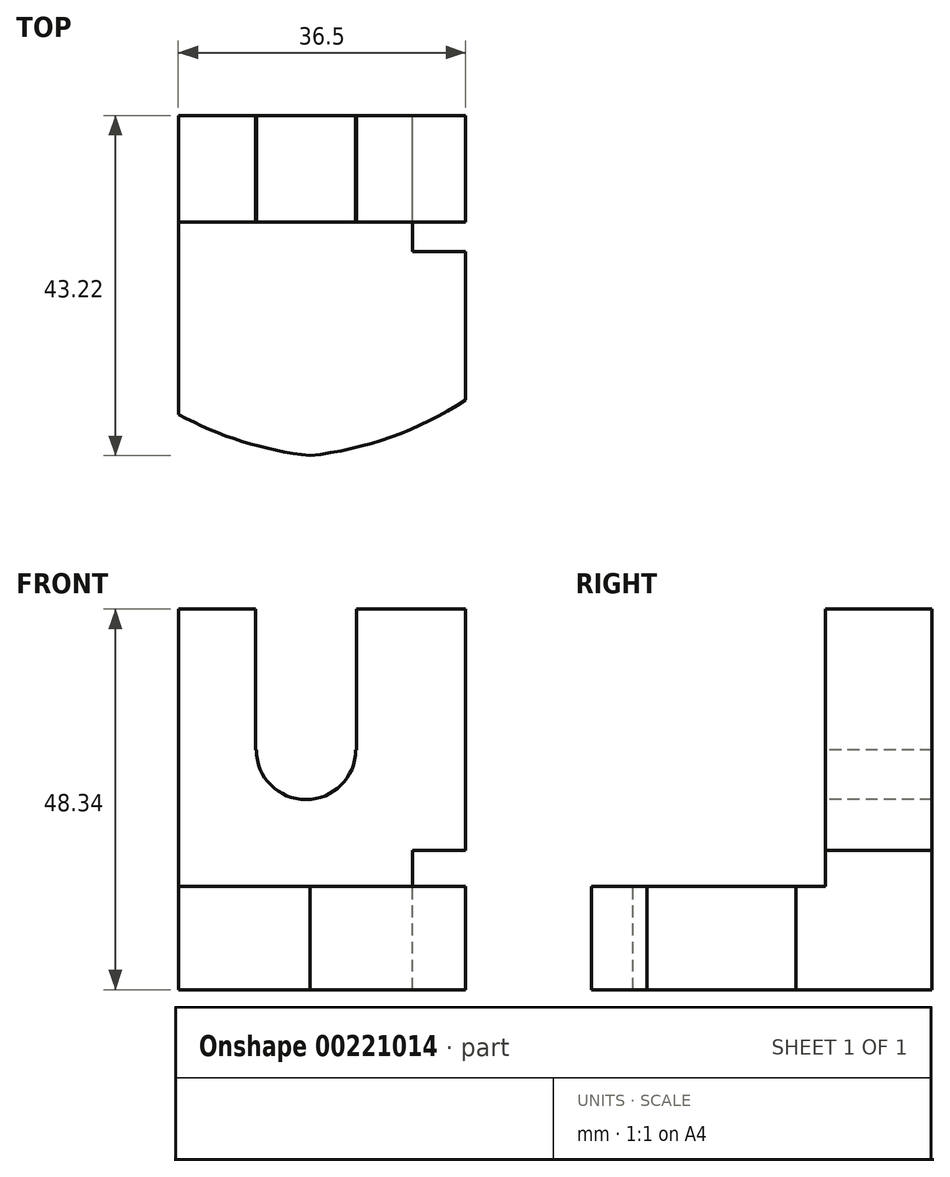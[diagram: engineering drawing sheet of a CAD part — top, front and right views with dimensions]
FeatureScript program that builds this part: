
annotation { "Feature Type Name" : "Feature", "Feature Type Description" : "" }
export const myFeature = defineFeature(function(context is Context, id is Id, definition is map)
    precondition{}
    {
        {
            var Q0;
            Q0=qCreatedBy(makeId("Top.planeOp"),FACE);
            var sketch = newSketch(context, id + "F0", { "sketchPlane" : qUnion([Q0])});
            skLineSegment(sketch, "E0.bottom", {"start": v(26.54, -21.75) * mm, "end": v(-26.54, -21.75) * mm});
            skLineSegment(sketch, "E0.top", {"start": v(26.54, 21.75) * mm, "end": v(-26.54, 21.75) * mm});
            skLineSegment(sketch, "E0.left", {"start": v(26.54, -21.75) * mm, "end": v(26.54, 21.75) * mm});
            skLineSegment(sketch, "E0.right", {"start": v(-26.54, -21.75) * mm, "end": v(-26.54, 21.75) * mm});
            skPoint(sketch, "E0.middle", {"position": v(0, 0) * mm});
            skSolve(sketch);
        }
        {
            var Q0;
            Q0 = qSketchRegion(id + "F0", true);
            var Q1;
            Q1=makeQuery(id+"F0.imprint","IMPRINT",FACE,{"disambiguationData":[TD([[makeQuery(id+"F0.imprint","IMPRINT",EDGE,{"derivedFrom":sQuery(id+"F0.wireOp",EDGE,"E0.bottom")}),-1.0]])]});
            extrude(context, id + "F1", {"entities" : qUnion([Q0, Q1]), "depth" : 48.34 * mm});
        }
        {
            var Q0;
            Q0=makeQuery(id+"F1.opExtrude","SWEPT_FACE",FACE,{"disambiguationData":[OSD([sQuery(id+"F0.wireOp",EDGE,"E0.left")])]});
            var sketch = newSketch(context, id + "F2", { "sketchPlane" : qUnion([Q0])});
            skLineSegment(sketch, "E1.bottom", {"start": v(-21.75, 13.12) * mm, "end": v(8.2, 13.12) * mm});
            skLineSegment(sketch, "E1.top", {"start": v(-21.75, 48.34) * mm, "end": v(8.2, 48.34) * mm});
            skLineSegment(sketch, "E1.left", {"start": v(-21.75, 13.12) * mm, "end": v(-21.75, 48.34) * mm});
            skLineSegment(sketch, "E1.right", {"start": v(8.2, 13.12) * mm, "end": v(8.2, 48.34) * mm});
            skSolve(sketch);
        }
        {
            var Q0;
            Q0=makeQuery(id+"F2.imprint","IMPRINT",FACE,{"disambiguationData":[TD([[makeQuery(id+"F2.imprint","IMPRINT",EDGE,{"derivedFrom":sQuery(id+"F2.wireOp",EDGE,"E1.bottom")}),1.0]])]});
            extrude(context, id + "F3", {"entities" : qUnion([Q0]), "operationType" : NewBodyOperationType.REMOVE, "endBound" : BoundingType.THROUGH_ALL, "oppositeDirection" : true, "depth" : 25.4 * mm});
        }
        {
            var Q0;
            Q0=makeQuery(id+"F3.boolean.opBoolean","COPY",FACE,{"derivedFrom":makeQuery(id+"F3.opExtrude","SWEPT_FACE",FACE,{"disambiguationData":[OSD([sQuery(id+"F2.wireOp",EDGE,"E1.right")])]})});
            var sketch = newSketch(context, id + "F11", { "sketchPlane" : qUnion([Q0])});
            skLineSegment(sketch, "E2.bottom", {"start": v(-6.91, 48.34) * mm, "end": v(5.89, 48.34) * mm});
            skLineSegment(sketch, "E2.top", {"start": v(-6.91, 30.46) * mm, "end": v(5.89, 30.46) * mm});
            skLineSegment(sketch, "E2.left", {"start": v(-6.91, 48.34) * mm, "end": v(-6.91, 30.46) * mm});
            skLineSegment(sketch, "E2.right", {"start": v(5.89, 48.34) * mm, "end": v(5.89, 30.46) * mm});
            skSolve(sketch);
        }
        {
            var Q0;
            Q0 = qSketchRegion(id + "F11", true);
            var Q1;
            Q1=makeQuery(id+"F11.imprint","IMPRINT",FACE,{"disambiguationData":[TD([[makeQuery(id+"F11.imprint","IMPRINT",EDGE,{"derivedFrom":sQuery(id+"F11.wireOp",EDGE,"E2.bottom")}),-1.0]])]});
            extrude(context, id + "F12", {"entities" : qUnion([Q0, Q1]), "operationType" : NewBodyOperationType.REMOVE, "endBound" : BoundingType.THROUGH_ALL, "oppositeDirection" : true, "depth" : 25.4 * mm});
        }
        {
            var Q0;
            Q0=makeQuery(id+"F3.boolean.opBoolean","COPY",FACE,{"derivedFrom":makeQuery(id+"F3.opExtrude","SWEPT_FACE",FACE,{"disambiguationData":[OSD([sQuery(id+"F2.wireOp",EDGE,"E1.right")])]})});
            var sketch = newSketch(context, id + "F13", { "sketchPlane" : qUnion([Q0])});
            skCircle(sketch, "E3", {"center": v(-0.51, 30.46) * mm, "radius": 6.31 * mm});
            skSolve(sketch);
        }
        {
            var Q0;
            Q0 = qSketchRegion(id + "F13", true);
            extrude(context, id + "F4", {"entities" : qUnion([Q0]), "operationType" : NewBodyOperationType.REMOVE, "endBound" : BoundingType.THROUGH_ALL, "oppositeDirection" : true, "depth" : 25.4 * mm});
        }
        {
            var Q0;
            Q0=makeQuery(id+"F1.opExtrude","SWEPT_EDGE",EDGE,{"disambiguationData":[OSD([sQuery(id+"F0.wireOp",EDGE,"E0.bottom"),sQuery(id+"F0.wireOp",EDGE,"E0.left")])]});
            var Q1;
            Q1=makeQuery(id+"F1.opExtrude","SWEPT_EDGE",EDGE,{"disambiguationData":[OSD([sQuery(id+"F0.wireOp",EDGE,"E0.bottom"),sQuery(id+"F0.wireOp",EDGE,"E0.right")])]});
            chamfer(context, id + "F5", {"entities" : qUnion([Q0, Q1]), "width" : 12.7 * mm, "tangentPropagation" : true});
        }
        {
            var Q0;
            {var subQ0=sQuery(id+"F0.wireOp",EDGE,"E0.bottom");Q0=makeQuery(id+"F5.opChamfer","BLEND_EDGE",EDGE,{"blendedFrom":[makeQuery(id+"F1.opExtrude","SWEPT_EDGE",EDGE,{"disambiguationData":[OSD([subQ0,sQuery(id+"F0.wireOp",EDGE,"E0.right")])]}),makeQuery(id+"F1.opExtrude","SWEPT_FACE",FACE,{"disambiguationData":[OSD([subQ0])]})],"blendedInto":[makeQuery(id+"F1.opExtrude","SWEPT_FACE",FACE,{"disambiguationData":[OSD([subQ0])]})]});}
            var Q1;
            {var subQ0=sQuery(id+"F0.wireOp",EDGE,"E0.bottom");Q1=makeQuery(id+"F5.opChamfer","BLEND_EDGE",EDGE,{"blendedFrom":[makeQuery(id+"F1.opExtrude","SWEPT_EDGE",EDGE,{"disambiguationData":[OSD([subQ0,sQuery(id+"F0.wireOp",EDGE,"E0.left")])]}),makeQuery(id+"F1.opExtrude","SWEPT_FACE",FACE,{"disambiguationData":[OSD([subQ0])]})],"blendedInto":[makeQuery(id+"F1.opExtrude","SWEPT_FACE",FACE,{"disambiguationData":[OSD([subQ0])]})]});}
            fillet(context, id + "F14", {"entities" : qUnion([Q0, Q1]), "radius" : 45.67 * mm, "tangentPropagation" : true, "allowEdgeOverflow" : false});
        }
        {
            var Q0;
            Q0=makeQuery(id+"F1.opExtrude","SWEPT_FACE",FACE,{"disambiguationData":[OSD([sQuery(id+"F0.wireOp",EDGE,"E0.top")])]});
            var sketch = newSketch(context, id + "F6", { "sketchPlane" : qUnion([Q0])});
            skLineSegment(sketch, "E4.bottom", {"start": v(-26.54, 0) * mm, "end": v(-12.99, 0) * mm});
            skLineSegment(sketch, "E4.top", {"start": v(-26.54, 17.67) * mm, "end": v(-12.99, 17.67) * mm});
            skLineSegment(sketch, "E4.left", {"start": v(-26.54, 0) * mm, "end": v(-26.54, 17.67) * mm});
            skLineSegment(sketch, "E4.right", {"start": v(-12.99, 0) * mm, "end": v(-12.99, 17.67) * mm});
            skSolve(sketch);
        }
        {
            var Q0;
            Q0=makeQuery(id+"F6.imprint","IMPRINT",FACE,{"disambiguationData":[TD([[makeQuery(id+"F6.imprint","IMPRINT",EDGE,{"derivedFrom":sQuery(id+"F6.wireOp",EDGE,"E4.bottom")}),1.0]])]});
            extrude(context, id + "F15", {"entities" : qUnion([Q0]), "operationType" : NewBodyOperationType.REMOVE, "oppositeDirection" : true, "depth" : 17.3 * mm});
        }
        {
            var Q0;
            Q0=makeQuery(id+"F1.opExtrude","SWEPT_FACE",FACE,{"disambiguationData":[OSD([sQuery(id+"F0.wireOp",EDGE,"E0.top")])]});
            var sketch = newSketch(context, id + "F7", { "sketchPlane" : qUnion([Q0])});
            skLineSegment(sketch, "E5.bottom", {"start": v(-26.54, 48.34) * mm, "end": v(-26.54, 48.34) * mm});
            skLineSegment(sketch, "E5.top", {"start": v(-26.54, 48.34) * mm, "end": v(-26.54, 48.34) * mm});
            skLineSegment(sketch, "E5.left", {"start": v(-26.54, 48.34) * mm, "end": v(-26.54, 48.34) * mm});
            skLineSegment(sketch, "E5.right", {"start": v(-26.54, 48.34) * mm, "end": v(-26.54, 48.34) * mm});
            skPoint(sketch, "E6.oppositeSnap0", {"position": v(-19.77, 17.67) * mm});
            skLineSegment(sketch, "E6.bottom", {"start": v(-26.54, 48.34) * mm, "end": v(-19.77, 48.34) * mm});
            skLineSegment(sketch, "E6.top", {"start": v(-26.54, 0) * mm, "end": v(-19.77, 0) * mm});
            skLineSegment(sketch, "E6.left", {"start": v(-26.54, 48.34) * mm, "end": v(-26.54, 0) * mm});
            skLineSegment(sketch, "E6.right", {"start": v(-19.77, 48.34) * mm, "end": v(-19.77, 0) * mm});
            skPoint(sketch, "E7.oppositeSnap0", {"position": v(16.73, 48.34) * mm});
            skLineSegment(sketch, "E7.bottom", {"start": v(26.54, 48.34) * mm, "end": v(16.73, 48.34) * mm});
            skLineSegment(sketch, "E7.top", {"start": v(26.54, 0) * mm, "end": v(16.73, 0) * mm});
            skLineSegment(sketch, "E7.left", {"start": v(26.54, 48.34) * mm, "end": v(26.54, 0) * mm});
            skLineSegment(sketch, "E7.right", {"start": v(16.73, 48.34) * mm, "end": v(16.73, 0) * mm});
            skSolve(sketch);
        }
        {
            var Q0;
            {var subQ0=sQuery(id+"F7.wireOp",EDGE,"E6.bottom");Q0=makeQuery(id+"F7.imprint","IMPRINT",FACE,{"disambiguationData":[TD([[makeQuery(id+"F7.imprint","IMPRINT",EDGE,{"derivedFrom":subQ0}),-1.0]])]});}
            var Q1;
            Q1=makeQuery(id+"F7.imprint","IMPRINT",FACE,{"disambiguationData":[TD([[makeQuery(id+"F7.imprint","IMPRINT",EDGE,{"derivedFrom":sQuery(id+"F7.wireOp",EDGE,"E7.bottom")}),-1.0]])]});
            extrude(context, id + "F8", {"entities" : qUnion([Q0, Q1]), "operationType" : NewBodyOperationType.REMOVE, "endBound" : BoundingType.THROUGH_ALL, "oppositeDirection" : true, "depth" : 25.4 * mm});
        }
        {
            var Q0;
            Q0=makeQuery(id+"F15.boolean.opBoolean","COPY",FACE,{"derivedFrom":makeQuery(id+"F15.opExtrude","CAP_FACE",FACE,{"disambiguationData":[OSD([sQuery(id+"F6.wireOp",EDGE,"E4.bottom"),sQuery(id+"F6.wireOp",EDGE,"E4.top"),sQuery(id+"F6.wireOp",EDGE,"E4.left"),sQuery(id+"F6.wireOp",EDGE,"E4.right")])],"isStart":false})});
            var sketch = newSketch(context, id + "F9", { "sketchPlane" : qUnion([Q0])});
            skLineSegment(sketch, "E8.bottom", {"start": v(-26.54, 13.12) * mm, "end": v(-19.77, 13.12) * mm});
            skLineSegment(sketch, "E8.top", {"start": v(-26.54, 0) * mm, "end": v(-19.77, 0) * mm});
            skLineSegment(sketch, "E8.left", {"start": v(-26.54, 13.12) * mm, "end": v(-26.54, 0) * mm});
            skLineSegment(sketch, "E8.right", {"start": v(-19.77, 13.12) * mm, "end": v(-19.77, 0) * mm});
            skSolve(sketch);
        }
        {
            var Q0;
            Q0=makeQuery(id+"F9.imprint","IMPRINT",FACE,{"disambiguationData":[TD([[makeQuery(id+"F9.imprint","IMPRINT",EDGE,{"derivedFrom":sQuery(id+"F9.wireOp",EDGE,"E8.bottom")}),1.0]])]});
            extrude(context, id + "F10", {"entities" : qUnion([Q0]), "operationType" : NewBodyOperationType.REMOVE, "endBound" : BoundingType.THROUGH_ALL, "oppositeDirection" : true, "depth" : 25.4 * mm});
        }
    });
